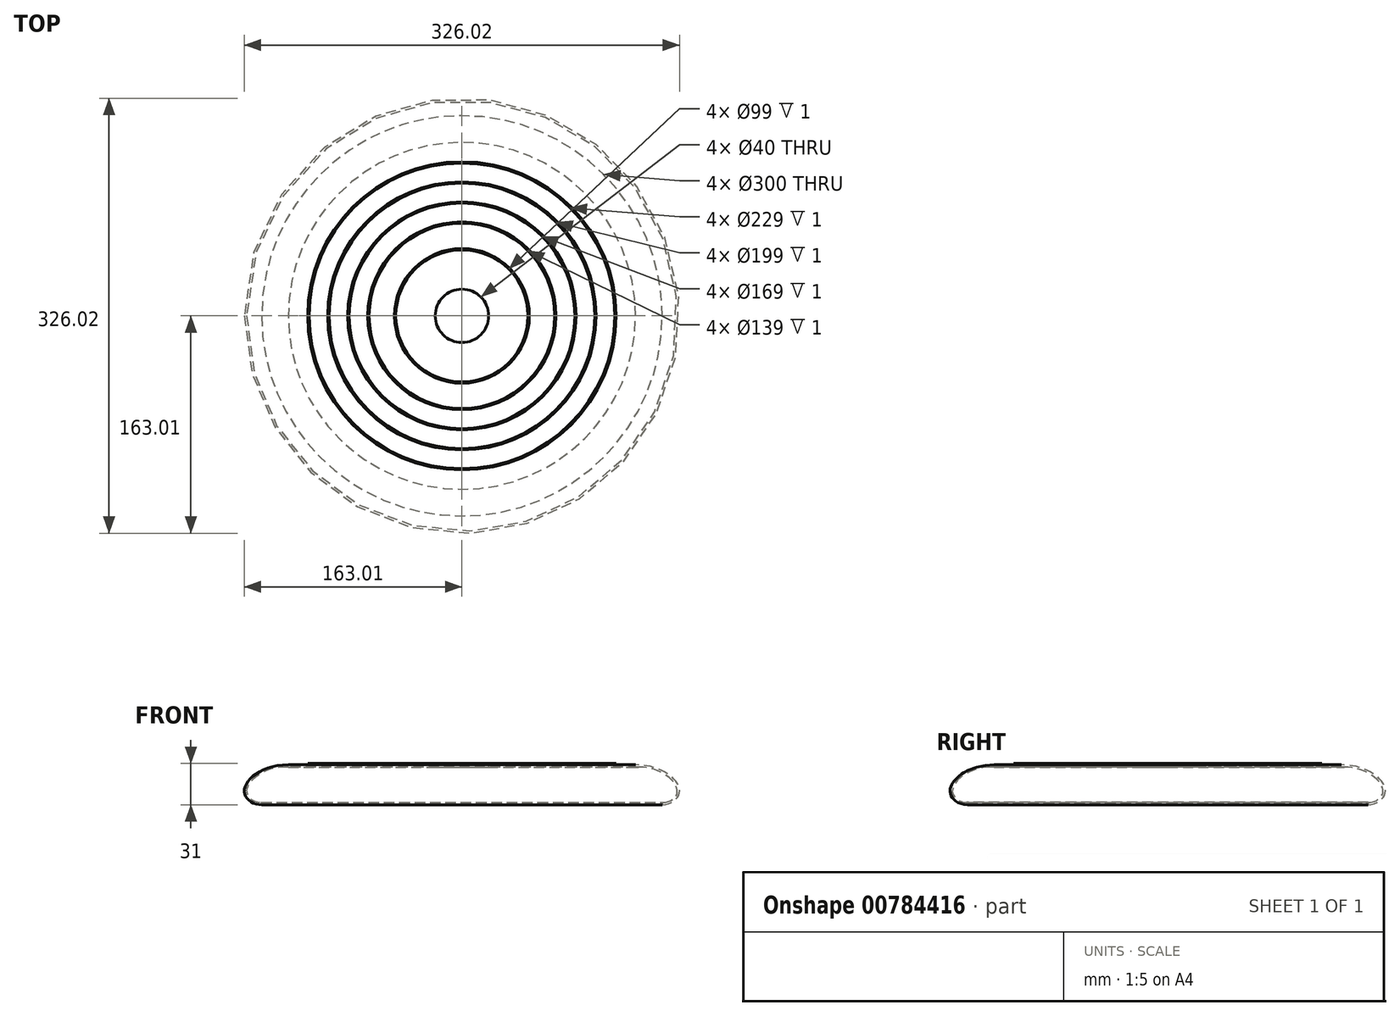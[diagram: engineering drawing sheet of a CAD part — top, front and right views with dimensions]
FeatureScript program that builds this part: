
annotation { "Feature Type Name" : "Feature", "Feature Type Description" : "" }
export const myFeature = defineFeature(function(context is Context, id is Id, definition is map)
    precondition{}
    {
        {
            var Q0;
            Q0=qCreatedBy(makeId("Front.planeOp"),FACE);
            var sketch = newSketch(context, id + "F0", { "sketchPlane" : qUnion([Q0])});
            skLineSegment(sketch, "E0", {"start": v(0, 0) * mm, "end": v(0, 30) * mm, "construction": true});
            skLineSegment(sketch, "E1", {"start": v(0, 0) * mm, "end": v(150, 0) * mm, "construction": true});
            skFitSpline(sketch, "E2", {"points": [v(130, 30) * mm, v(163, 10) * mm, v(150, 0) * mm], "startDerivative": vector(99.12, 0) * mm, "endDerivative": vector(-50.48, 0) * mm});
            skLineSegment(sketch, "E3", {"start": v(150, 1.75) * mm, "end": v(150, 0) * mm});
            skFitSpline(sketch, "E4.0", {"points": [v(130, 28.25) * mm, v(134, 28.25) * mm, v(141.41, 27.3) * mm, v(148.97, 24.41) * mm, v(153.8, 21.44) * mm, v(156.76, 19) * mm, v(159.02, 16.45) * mm, v(160.27, 14.33) * mm, v(160.9, 12.72) * mm, v(161.18, 11.56) * mm, v(161.29, 10.46) * mm, v(161.22, 9.43) * mm, v(160.98, 8.43) * mm, v(160.46, 7.14) * mm, v(159.41, 5.6) * mm, v(157.6, 4.01) * mm, v(155.35, 2.76) * mm, v(152.77, 1.95) * mm, v(150.93, 1.75) * mm, v(150, 1.75) * mm]});
            skLineSegment(sketch, "E5", {"start": v(49.5, 30) * mm, "end": v(49.5, 31) * mm});
            skLineSegment(sketch, "E6", {"start": v(49.5, 31) * mm, "end": v(50.5, 31) * mm});
            skLineSegment(sketch, "E7", {"start": v(50.5, 31) * mm, "end": v(50.5, 30) * mm});
            skLineSegment(sketch, "E8", {"start": v(50.5, 30) * mm, "end": v(69.5, 30) * mm});
            skLineSegment(sketch, "E9", {"start": v(69.5, 30) * mm, "end": v(69.5, 31) * mm});
            skLineSegment(sketch, "E10", {"start": v(69.5, 31) * mm, "end": v(70.5, 31) * mm});
            skLineSegment(sketch, "E11", {"start": v(70.5, 31) * mm, "end": v(70.5, 30) * mm});
            skLineSegment(sketch, "E12", {"start": v(70.5, 30) * mm, "end": v(84.5, 30) * mm});
            skLineSegment(sketch, "E13", {"start": v(84.5, 30) * mm, "end": v(84.5, 31) * mm});
            skLineSegment(sketch, "E14", {"start": v(84.5, 31) * mm, "end": v(85.5, 31) * mm});
            skLineSegment(sketch, "E15", {"start": v(85.5, 31) * mm, "end": v(85.5, 30) * mm});
            skLineSegment(sketch, "E16", {"start": v(85.5, 30) * mm, "end": v(99.5, 30) * mm});
            skLineSegment(sketch, "E17", {"start": v(99.5, 30) * mm, "end": v(99.5, 31) * mm});
            skLineSegment(sketch, "E18", {"start": v(99.5, 31) * mm, "end": v(100.5, 31) * mm});
            skLineSegment(sketch, "E19", {"start": v(100.5, 31) * mm, "end": v(100.5, 30) * mm});
            skLineSegment(sketch, "E20", {"start": v(100.5, 30) * mm, "end": v(114.5, 30) * mm});
            skLineSegment(sketch, "E21", {"start": v(114.5, 30) * mm, "end": v(114.5, 31) * mm});
            skLineSegment(sketch, "E22", {"start": v(114.5, 31) * mm, "end": v(115.5, 31) * mm});
            skLineSegment(sketch, "E23", {"start": v(115.5, 31) * mm, "end": v(115.5, 30) * mm});
            skLineSegment(sketch, "E24", {"start": v(115.5, 30) * mm, "end": v(130, 30) * mm});
            skLineSegment(sketch, "E25", {"start": v(50, 31) * mm, "end": v(50, 28.25) * mm, "construction": true});
            skLineSegment(sketch, "E26", {"start": v(70, 31) * mm, "end": v(70, 28.25) * mm, "construction": true});
            skLineSegment(sketch, "E27", {"start": v(85, 31) * mm, "end": v(85, 28.25) * mm, "construction": true});
            skLineSegment(sketch, "E28", {"start": v(100, 31) * mm, "end": v(100, 28.25) * mm, "construction": true});
            skLineSegment(sketch, "E29", {"start": v(115, 31) * mm, "end": v(115, 28.25) * mm, "construction": true});
            skLineSegment(sketch, "E30", {"start": v(20, 30) * mm, "end": v(20, 30) * mm});
            skLineSegment(sketch, "E31", {"start": v(20, 30) * mm, "end": v(20, 28.25) * mm});
            skLineSegment(sketch, "E32", {"start": v(20, 28.25) * mm, "end": v(20, 28.25) * mm});
            skLineSegment(sketch, "E33", {"start": v(20, 28.25) * mm, "end": v(130, 28.25) * mm});
            skLineSegment(sketch, "E34", {"start": v(20, 30) * mm, "end": v(49.5, 30) * mm});
            skSolve(sketch);
        }
        {
            var Q0;
            Q0=makeQuery(id+"F0.imprint","IMPRINT",FACE,{"disambiguationData":[TD([[makeQuery(id+"F0.imprint","IMPRINT",EDGE,{"derivedFrom":sQuery(id+"F0.wireOp",EDGE,"E2")}),-1.0]])]});
            var Q1;
            Q1=sQuery(id+"F0.wireOp",EDGE,"E0");
            revolve(context, id + "F1", {"surfaceOperationType" : NewSurfaceOperationType.NEW, "entities" : qUnion([Q0]), "axis" : qUnion([Q1]), "revolveType" : RevolveType.FULL});
        }
    });
